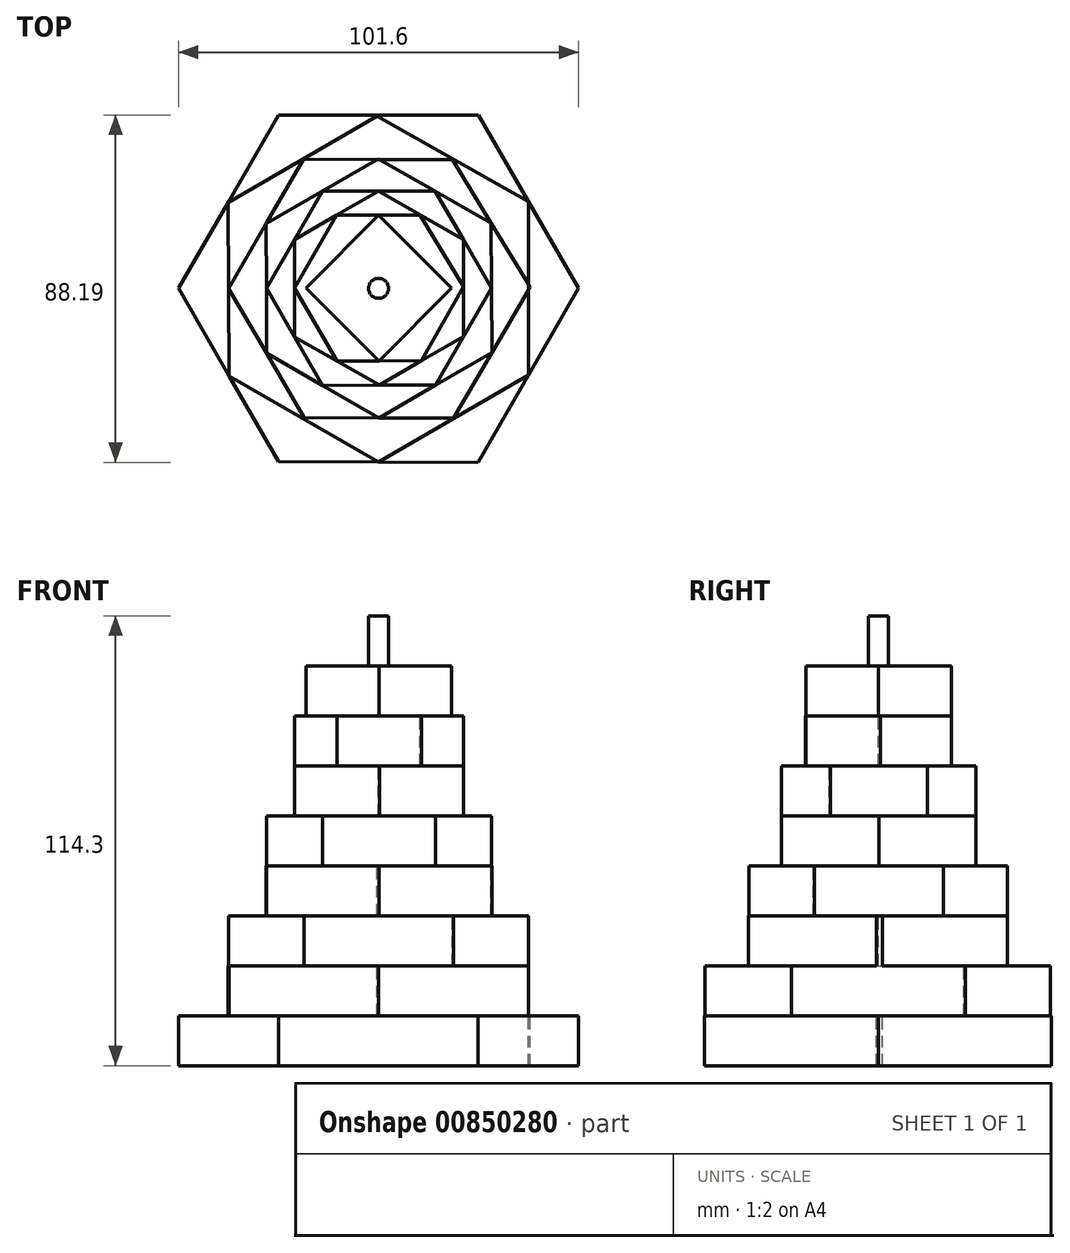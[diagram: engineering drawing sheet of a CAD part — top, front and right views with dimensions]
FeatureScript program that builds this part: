
annotation { "Feature Type Name" : "Feature", "Feature Type Description" : "" }
export const myFeature = defineFeature(function(context is Context, id is Id, definition is map)
    precondition{}
    {
        {
            var Q0;
            Q0=qCreatedBy(makeId("Top.planeOp"),FACE);
            var sketch = newSketch(context, id + "F0", { "sketchPlane" : qUnion([Q0])});
            skLineSegment(sketch, "E0.0", {"start": v(-25.4, 44) * mm, "end": v(25.4, 44) * mm});
            skLineSegment(sketch, "E0.1", {"start": v(25.4, 44) * mm, "end": v(50.8, 0) * mm});
            skLineSegment(sketch, "E0.2", {"start": v(50.8, 0) * mm, "end": v(25.22, -44.2) * mm});
            skLineSegment(sketch, "E0.3", {"start": v(25.22, -44.2) * mm, "end": v(-25.4, -44) * mm});
            skLineSegment(sketch, "E0.4", {"start": v(-25.4, -44) * mm, "end": v(-50.8, 0) * mm});
            skLineSegment(sketch, "E0.5", {"start": v(-50.8, 0) * mm, "end": v(-25.4, 44) * mm});
            skPoint(sketch, "E0.0.midPoint", {"position": v(0, 44) * mm});
            skLineSegment(sketch, "E1.0", {"start": v(-0.34, 43.7) * mm, "end": v(38.07, 22.05) * mm});
            skLineSegment(sketch, "E1.1", {"start": v(38.07, 22.05) * mm, "end": v(38.05, -22.04) * mm});
            skLineSegment(sketch, "E1.2", {"start": v(38.05, -22.04) * mm, "end": v(0.03, -44.1) * mm});
            skLineSegment(sketch, "E1.3", {"start": v(0.03, -44.1) * mm, "end": v(-37.96, -22.24) * mm});
            skLineSegment(sketch, "E1.4", {"start": v(-37.96, -22.24) * mm, "end": v(-38.26, 21.72) * mm});
            skLineSegment(sketch, "E1.5", {"start": v(-38.26, 21.72) * mm, "end": v(-0.34, 43.7) * mm});
            skPoint(sketch, "E1.0.midPoint", {"position": v(18.87, 32.87) * mm});
            skLineSegment(sketch, "E2.0", {"start": v(-19.09, 32.78) * mm, "end": v(18.8, 32.73) * mm});
            skLineSegment(sketch, "E2.1", {"start": v(18.8, 32.73) * mm, "end": v(38.5, 0.3) * mm});
            skLineSegment(sketch, "E2.2", {"start": v(38.5, 0.3) * mm, "end": v(19.06, -33.01) * mm});
            skLineSegment(sketch, "E2.3", {"start": v(19.06, -33.01) * mm, "end": v(-18.96, -32.83) * mm});
            skLineSegment(sketch, "E2.4", {"start": v(-18.96, -32.83) * mm, "end": v(-38.05, -0.06) * mm});
            skLineSegment(sketch, "E2.5", {"start": v(-38.05, -0.06) * mm, "end": v(-19.09, 32.78) * mm});
            skPoint(sketch, "E2.0.midPoint", {"position": v(-0.14, 32.75) * mm});
            skLineSegment(sketch, "E3.0", {"start": v(-28.53, 16.43) * mm, "end": v(-0.03, 32.94) * mm});
            skLineSegment(sketch, "E3.1", {"start": v(-0.03, 32.94) * mm, "end": v(28.62, 16.57) * mm});
            skLineSegment(sketch, "E3.2", {"start": v(28.62, 16.57) * mm, "end": v(28.82, -16.28) * mm});
            skLineSegment(sketch, "E3.3", {"start": v(28.82, -16.28) * mm, "end": v(0.07, -32.92) * mm});
            skLineSegment(sketch, "E3.4", {"start": v(0.07, -32.92) * mm, "end": v(-28.48, -16.5) * mm});
            skLineSegment(sketch, "E3.5", {"start": v(-28.48, -16.5) * mm, "end": v(-28.53, 16.43) * mm});
            skPoint(sketch, "E3.0.midPoint", {"position": v(-14.28, 24.69) * mm});
            skLineSegment(sketch, "E4.0", {"start": v(-14.2, 24.72) * mm, "end": v(14.35, 24.72) * mm});
            skLineSegment(sketch, "E4.1", {"start": v(14.35, 24.72) * mm, "end": v(28.72, 0.09) * mm});
            skLineSegment(sketch, "E4.2", {"start": v(28.72, 0.09) * mm, "end": v(14.47, -24.59) * mm});
            skLineSegment(sketch, "E4.3", {"start": v(14.47, -24.59) * mm, "end": v(-14.24, -24.69) * mm});
            skLineSegment(sketch, "E4.4", {"start": v(-14.24, -24.69) * mm, "end": v(-28.5, 0.02) * mm});
            skLineSegment(sketch, "E4.5", {"start": v(-28.5, 0.02) * mm, "end": v(-14.2, 24.72) * mm});
            skPoint(sketch, "E4.0.midPoint", {"position": v(0.08, 24.72) * mm});
            skLineSegment(sketch, "E5.0", {"start": v(0.02, 24.73) * mm, "end": v(21.52, 12.43) * mm});
            skLineSegment(sketch, "E5.1", {"start": v(21.52, 12.43) * mm, "end": v(21.6, -12.25) * mm});
            skLineSegment(sketch, "E5.2", {"start": v(21.6, -12.25) * mm, "end": v(0.2, -24.64) * mm});
            skLineSegment(sketch, "E5.3", {"start": v(0.2, -24.64) * mm, "end": v(-21.33, -12.4) * mm});
            skLineSegment(sketch, "E5.4", {"start": v(-21.33, -12.4) * mm, "end": v(-21.38, 12.32) * mm});
            skLineSegment(sketch, "E5.5", {"start": v(-21.38, 12.32) * mm, "end": v(0.02, 24.73) * mm});
            skPoint(sketch, "E5.0.midPoint", {"position": v(10.77, 18.58) * mm});
            skLineSegment(sketch, "E6.0", {"start": v(-10.63, 18.55) * mm, "end": v(10.57, 18.57) * mm});
            skLineSegment(sketch, "E6.1", {"start": v(10.57, 18.57) * mm, "end": v(21.56, 0.46) * mm});
            skLineSegment(sketch, "E6.2", {"start": v(21.56, 0.46) * mm, "end": v(10.94, -18.41) * mm});
            skLineSegment(sketch, "E6.3", {"start": v(10.94, -18.41) * mm, "end": v(-10.58, -18.52) * mm});
            skLineSegment(sketch, "E6.4", {"start": v(-10.58, -18.52) * mm, "end": v(-21.35, 0.03) * mm});
            skLineSegment(sketch, "E6.5", {"start": v(-21.35, 0.03) * mm, "end": v(-10.63, 18.55) * mm});
            skPoint(sketch, "E6.0.midPoint", {"position": v(-0.03, 18.56) * mm});
            skPoint(sketch, "E7.endSnap0", {"position": v(0.18, -18.46) * mm});
            skLineSegment(sketch, "E8.0", {"start": v(-0.03, 18.56) * mm, "end": v(18.59, 0.01) * mm});
            skLineSegment(sketch, "E8.1", {"start": v(18.59, 0.01) * mm, "end": v(0.18, -18.46) * mm});
            skLineSegment(sketch, "E8.2", {"start": v(0.18, -18.46) * mm, "end": v(-18.44, 0.09) * mm});
            skLineSegment(sketch, "E8.3", {"start": v(-18.44, 0.09) * mm, "end": v(-0.03, 18.56) * mm});
            skPoint(sketch, "E9", {"position": v(0, 0) * mm});
            skCircle(sketch, "E10", {"center": v(0, 0) * mm, "radius": 2.54 * mm});
            skSolve(sketch);
        }
        {
            var Q0;
            {var subQ3=sQuery(id+"F0.wireOp",EDGE,"E1.3");Q0=makeQuery(id+"F0.imprint","IMPRINT",FACE,{"disambiguationData":[TD([[makeQuery(id+"F0.imprint","IMPRINT",EDGE,{"derivedFrom":subQ3}),1.0]])]});}
            var Q1;
            {var subQ3=sQuery(id+"F0.wireOp",EDGE,"E1.2");Q1=makeQuery(id+"F0.imprint","IMPRINT",FACE,{"disambiguationData":[TD([[makeQuery(id+"F0.imprint","IMPRINT",EDGE,{"derivedFrom":subQ3}),1.0]])]});}
            var Q2;
            {var subQ11=sQuery(id+"F0.wireOp",EDGE,"E1.0");Q2=makeQuery(id+"F0.imprint","IMPRINT",FACE,{"disambiguationData":[TD([[makeQuery(id+"F0.imprint","IMPRINT",EDGE,{"derivedFrom":subQ11}),-1.0]])]});}
            var Q3;
            {var subQ0=sQuery(id+"F0.wireOp",EDGE,"E2.3");var subQ1=sQuery(id+"F0.wireOp",EDGE,"E2.2");var subQ2=makeQuery(id+"F0.imprint","INTERSECT",VERTEX,{"derivedFrom":[subQ1,subQ0]});Q3=makeQuery(id+"F0.imprint","IMPRINT",FACE,{"disambiguationData":[TD([[makeQuery(id+"F0.imprint","IMPRINT",EDGE,{"disambiguationData":[TD([[subQ2,1.0]])],"derivedFrom":subQ1}),-1.0]])]});}
            var Q4;
            {var subQ0=sQuery(id+"F0.wireOp",EDGE,"E2.4");var subQ1=sQuery(id+"F0.wireOp",EDGE,"E2.3");var subQ2=makeQuery(id+"F0.imprint","INTERSECT",VERTEX,{"derivedFrom":[subQ1,subQ0]});Q4=makeQuery(id+"F0.imprint","IMPRINT",FACE,{"disambiguationData":[TD([[makeQuery(id+"F0.imprint","IMPRINT",EDGE,{"disambiguationData":[TD([[subQ2,1.0]])],"derivedFrom":subQ1}),-1.0]])]});}
            var Q5;
            {var subQ0=sQuery(id+"F0.wireOp",EDGE,"E3.4");var subQ1=sQuery(id+"F0.wireOp",EDGE,"E3.3");var subQ2=makeQuery(id+"F0.imprint","INTERSECT",VERTEX,{"derivedFrom":[sQuery(id+"F0.wireOp",EDGE,"E2.3"),subQ1,subQ0]});Q5=makeQuery(id+"F0.imprint","IMPRINT",FACE,{"disambiguationData":[TD([[makeQuery(id+"F0.imprint","IMPRINT",EDGE,{"disambiguationData":[TD([[subQ2,1.0]])],"derivedFrom":subQ1}),-1.0]])]});}
            var Q6;
            {var subQ0=sQuery(id+"F0.wireOp",EDGE,"E4.4");var subQ1=sQuery(id+"F0.wireOp",EDGE,"E4.3");var subQ2=makeQuery(id+"F0.imprint","INTERSECT",VERTEX,{"derivedFrom":[sQuery(id+"F0.wireOp",EDGE,"E3.4"),subQ1,subQ0]});Q6=makeQuery(id+"F0.imprint","IMPRINT",FACE,{"disambiguationData":[TD([[makeQuery(id+"F0.imprint","IMPRINT",EDGE,{"disambiguationData":[TD([[subQ2,1.0]])],"derivedFrom":subQ1}),-1.0]])]});}
            var Q7;
            {var subQ0=sQuery(id+"F0.wireOp",EDGE,"E5.3");var subQ1=sQuery(id+"F0.wireOp",EDGE,"E5.2");var subQ2=makeQuery(id+"F0.imprint","INTERSECT",VERTEX,{"derivedFrom":[sQuery(id+"F0.wireOp",EDGE,"E4.3"),subQ1,subQ0]});Q7=makeQuery(id+"F0.imprint","IMPRINT",FACE,{"disambiguationData":[TD([[makeQuery(id+"F0.imprint","IMPRINT",EDGE,{"disambiguationData":[TD([[subQ2,1.0]])],"derivedFrom":subQ1}),-1.0]])]});}
            var Q8;
            {var subQ0=sQuery(id+"F0.wireOp",EDGE,"E4.3");var subQ1=sQuery(id+"F0.wireOp",EDGE,"E4.2");var subQ2=makeQuery(id+"F0.imprint","INTERSECT",VERTEX,{"derivedFrom":[sQuery(id+"F0.wireOp",EDGE,"E3.3"),subQ1,subQ0]});Q8=makeQuery(id+"F0.imprint","IMPRINT",FACE,{"disambiguationData":[TD([[makeQuery(id+"F0.imprint","IMPRINT",EDGE,{"disambiguationData":[TD([[subQ2,1.0]])],"derivedFrom":subQ1}),-1.0]])]});}
            var Q9;
            {var subQ3=sQuery(id+"F0.wireOp",EDGE,"E6.2");Q9=makeQuery(id+"F0.imprint","IMPRINT",FACE,{"disambiguationData":[TD([[makeQuery(id+"F0.imprint","IMPRINT",EDGE,{"derivedFrom":subQ3}),1.0]])]});}
            var Q10;
            {var subQ3=sQuery(id+"F0.wireOp",EDGE,"E6.1");Q10=makeQuery(id+"F0.imprint","IMPRINT",FACE,{"disambiguationData":[TD([[makeQuery(id+"F0.imprint","IMPRINT",EDGE,{"derivedFrom":subQ3}),-1.0]])]});}
            var Q11;
            {var subQ0=sQuery(id+"F0.wireOp",EDGE,"E3.3");var subQ1=sQuery(id+"F0.wireOp",EDGE,"E3.2");var subQ2=makeQuery(id+"F0.imprint","INTERSECT",VERTEX,{"derivedFrom":[sQuery(id+"F0.wireOp",EDGE,"E2.2"),subQ1,subQ0]});Q11=makeQuery(id+"F0.imprint","IMPRINT",FACE,{"disambiguationData":[TD([[makeQuery(id+"F0.imprint","IMPRINT",EDGE,{"disambiguationData":[TD([[subQ2,1.0]])],"derivedFrom":subQ1}),-1.0]])]});}
            var Q12;
            {var subQ0=sQuery(id+"F0.wireOp",EDGE,"E4.2");var subQ1=sQuery(id+"F0.wireOp",EDGE,"E4.1");var subQ2=makeQuery(id+"F0.imprint","INTERSECT",VERTEX,{"derivedFrom":[sQuery(id+"F0.wireOp",EDGE,"E3.2"),subQ1,subQ0]});Q12=makeQuery(id+"F0.imprint","IMPRINT",FACE,{"disambiguationData":[TD([[makeQuery(id+"F0.imprint","IMPRINT",EDGE,{"disambiguationData":[TD([[subQ2,1.0]])],"derivedFrom":subQ1}),-1.0]])]});}
            var Q13;
            {var subQ1=sQuery(id+"F0.wireOp",EDGE,"E2.1");var subQ6=sQuery(id+"F0.wireOp",EDGE,"E1.1");var subQ8=makeQuery(id+"F0.imprint","INTERSECT",VERTEX,{"derivedFrom":[subQ6,subQ1]});Q13=makeQuery(id+"F0.imprint","IMPRINT",FACE,{"disambiguationData":[TD([[makeQuery(id+"F0.imprint","IMPRINT",EDGE,{"disambiguationData":[TD([[subQ8,-1.0]])],"derivedFrom":subQ6}),-1.0]])]});}
            var Q14;
            {var subQ0=sQuery(id+"F0.wireOp",EDGE,"E3.2");var subQ1=sQuery(id+"F0.wireOp",EDGE,"E3.1");var subQ2=makeQuery(id+"F0.imprint","INTERSECT",VERTEX,{"derivedFrom":[sQuery(id+"F0.wireOp",EDGE,"E2.1"),subQ1,subQ0]});Q14=makeQuery(id+"F0.imprint","IMPRINT",FACE,{"disambiguationData":[TD([[makeQuery(id+"F0.imprint","IMPRINT",EDGE,{"disambiguationData":[TD([[subQ2,1.0]])],"derivedFrom":subQ1}),-1.0]])]});}
            var Q15;
            {var subQ0=sQuery(id+"F0.wireOp",EDGE,"E2.1");var subQ1=sQuery(id+"F0.wireOp",EDGE,"E2.0");var subQ2=makeQuery(id+"F0.imprint","INTERSECT",VERTEX,{"derivedFrom":[subQ1,subQ0]});Q15=makeQuery(id+"F0.imprint","IMPRINT",FACE,{"disambiguationData":[TD([[makeQuery(id+"F0.imprint","IMPRINT",EDGE,{"disambiguationData":[TD([[subQ2,1.0]])],"derivedFrom":subQ1}),-1.0]])]});}
            var Q16;
            {var subQ0=sQuery(id+"F0.wireOp",EDGE,"E2.5");var subQ1=sQuery(id+"F0.wireOp",EDGE,"E2.0");var subQ2=makeQuery(id+"F0.imprint","INTERSECT",VERTEX,{"derivedFrom":[subQ1,subQ0]});Q16=makeQuery(id+"F0.imprint","IMPRINT",FACE,{"disambiguationData":[TD([[makeQuery(id+"F0.imprint","IMPRINT",EDGE,{"disambiguationData":[TD([[subQ2,-1.0]])],"derivedFrom":subQ1}),-1.0]])]});}
            var Q17;
            {var subQ1=sQuery(id+"F0.wireOp",EDGE,"E3.0");var subQ8=sQuery(id+"F0.wireOp",EDGE,"E2.0");var subQ13=makeQuery(id+"F0.imprint","INTERSECT",VERTEX,{"derivedFrom":[subQ8,subQ1]});Q17=makeQuery(id+"F0.imprint","IMPRINT",FACE,{"disambiguationData":[TD([[makeQuery(id+"F0.imprint","IMPRINT",EDGE,{"disambiguationData":[TD([[subQ13,-1.0]])],"derivedFrom":subQ8}),-1.0]])]});}
            var Q18;
            {var subQ0=sQuery(id+"F0.wireOp",EDGE,"E4.5");var subQ1=sQuery(id+"F0.wireOp",EDGE,"E4.0");var subQ2=makeQuery(id+"F0.imprint","INTERSECT",VERTEX,{"derivedFrom":[subQ1,subQ0]});Q18=makeQuery(id+"F0.imprint","IMPRINT",FACE,{"disambiguationData":[TD([[makeQuery(id+"F0.imprint","IMPRINT",EDGE,{"disambiguationData":[TD([[subQ2,-1.0]])],"derivedFrom":subQ1}),-1.0]])]});}
            var Q19;
            {var subQ3=sQuery(id+"F0.wireOp",EDGE,"E6.5");Q19=makeQuery(id+"F0.imprint","IMPRINT",FACE,{"disambiguationData":[TD([[makeQuery(id+"F0.imprint","IMPRINT",EDGE,{"derivedFrom":subQ3}),1.0]])]});}
            var Q20;
            {var subQ1=sQuery(id+"F0.wireOp",EDGE,"E6.4");Q20=makeQuery(id+"F0.imprint","IMPRINT",FACE,{"disambiguationData":[TD([[makeQuery(id+"F0.imprint","IMPRINT",EDGE,{"derivedFrom":subQ1}),-1.0]])]});}
            var Q21;
            Q21=makeQuery(id+"F0.imprint","IMPRINT",FACE,{"disambiguationData":[TD([[makeQuery(id+"F0.imprint","IMPRINT",EDGE,{"derivedFrom":sQuery(id+"F0.wireOp",EDGE,"E8.0")}),-1.0]])]});
            var Q22;
            Q22=makeQuery(id+"F0.imprint","IMPRINT",FACE,{"disambiguationData":[TD([[makeQuery(id+"F0.imprint","IMPRINT",EDGE,{"derivedFrom":sQuery(id+"F0.wireOp",EDGE,"E10")}),1.0]])]});
            var Q23;
            {var subQ1=sQuery(id+"F0.wireOp",EDGE,"E4.0");var subQ3=sQuery(id+"F0.wireOp",EDGE,"E5.0");var subQ4=makeQuery(id+"F0.imprint","INTERSECT",VERTEX,{"derivedFrom":[subQ1,subQ3]});Q23=makeQuery(id+"F0.imprint","IMPRINT",FACE,{"disambiguationData":[TD([[makeQuery(id+"F0.imprint","IMPRINT",EDGE,{"disambiguationData":[TD([[subQ4,-1.0]])],"derivedFrom":subQ1}),-1.0]])]});}
            var Q24;
            {var subQ3=sQuery(id+"F0.wireOp",EDGE,"E6.1");Q24=makeQuery(id+"F0.imprint","IMPRINT",FACE,{"disambiguationData":[TD([[makeQuery(id+"F0.imprint","IMPRINT",EDGE,{"derivedFrom":subQ3}),1.0]])]});}
            var Q25;
            {var subQ0=sQuery(id+"F0.wireOp",EDGE,"E2.5");var subQ1=sQuery(id+"F0.wireOp",EDGE,"E2.4");var subQ2=makeQuery(id+"F0.imprint","INTERSECT",VERTEX,{"derivedFrom":[subQ1,subQ0]});Q25=makeQuery(id+"F0.imprint","IMPRINT",FACE,{"disambiguationData":[TD([[makeQuery(id+"F0.imprint","IMPRINT",EDGE,{"disambiguationData":[TD([[subQ2,1.0]])],"derivedFrom":subQ1}),-1.0]])]});}
            var Q26;
            {var subQ0=sQuery(id+"F0.wireOp",EDGE,"E3.5");var subQ1=sQuery(id+"F0.wireOp",EDGE,"E3.4");var subQ2=makeQuery(id+"F0.imprint","INTERSECT",VERTEX,{"derivedFrom":[sQuery(id+"F0.wireOp",EDGE,"E2.4"),subQ1,subQ0]});Q26=makeQuery(id+"F0.imprint","IMPRINT",FACE,{"disambiguationData":[TD([[makeQuery(id+"F0.imprint","IMPRINT",EDGE,{"disambiguationData":[TD([[subQ2,1.0]])],"derivedFrom":subQ1}),-1.0]])]});}
            var Q27;
            {var subQ0=sQuery(id+"F0.wireOp",EDGE,"E4.5");var subQ1=sQuery(id+"F0.wireOp",EDGE,"E4.4");var subQ2=makeQuery(id+"F0.imprint","INTERSECT",VERTEX,{"derivedFrom":[sQuery(id+"F0.wireOp",EDGE,"E3.5"),subQ1,subQ0]});Q27=makeQuery(id+"F0.imprint","IMPRINT",FACE,{"disambiguationData":[TD([[makeQuery(id+"F0.imprint","IMPRINT",EDGE,{"disambiguationData":[TD([[subQ2,1.0]])],"derivedFrom":subQ1}),-1.0]])]});}
            var Q28;
            {var subQ3=sQuery(id+"F0.wireOp",EDGE,"E6.4");Q28=makeQuery(id+"F0.imprint","IMPRINT",FACE,{"disambiguationData":[TD([[makeQuery(id+"F0.imprint","IMPRINT",EDGE,{"derivedFrom":subQ3}),1.0]])]});}
            var Q29;
            {var subQ3=sQuery(id+"F0.wireOp",EDGE,"E1.4");Q29=makeQuery(id+"F0.imprint","IMPRINT",FACE,{"disambiguationData":[TD([[makeQuery(id+"F0.imprint","IMPRINT",EDGE,{"derivedFrom":subQ3}),1.0]])]});}
            var Q30;
            {var subQ3=sQuery(id+"F0.wireOp",EDGE,"E2.2");var subQ7=sQuery(id+"F0.wireOp",EDGE,"E2.1");var subQ8=makeQuery(id+"F0.imprint","INTERSECT",VERTEX,{"derivedFrom":[subQ7,subQ3]});Q30=makeQuery(id+"F0.imprint","IMPRINT",FACE,{"disambiguationData":[TD([[makeQuery(id+"F0.imprint","IMPRINT",EDGE,{"disambiguationData":[TD([[subQ8,1.0]])],"derivedFrom":subQ7}),1.0]])]});}
            var Q31;
            {var subQ1=sQuery(id+"F0.wireOp",EDGE,"E0.0");Q31=makeQuery(id+"F0.imprint","IMPRINT",FACE,{"disambiguationData":[TD([[makeQuery(id+"F0.imprint","IMPRINT",EDGE,{"derivedFrom":subQ1}),-1.0]])]});}
            extrude(context, id + "F1", {"entities" : qUnion([Q0, Q1, Q2, Q3, Q4, Q5, Q6, Q7, Q8, Q9, Q10, Q11, Q12, Q13, Q14, Q15, Q16, Q17, Q18, Q19, Q20, Q21, Q22, Q23, Q24, Q25, Q26, Q27, Q28, Q29, Q30, Q31]), "oppositeDirection" : true, "depth" : 114.3 * mm, "offsetDistance" : 25.4 * mm});
        }
        {
            var Q0;
            {var subQ1=sQuery(id+"F0.wireOp",EDGE,"E0.0");Q0=makeQuery(id+"F0.imprint","IMPRINT",FACE,{"disambiguationData":[TD([[makeQuery(id+"F0.imprint","IMPRINT",EDGE,{"derivedFrom":subQ1}),-1.0]])]});}
            var Q1;
            {var subQ3=sQuery(id+"F0.wireOp",EDGE,"E1.2");Q1=makeQuery(id+"F0.imprint","IMPRINT",FACE,{"disambiguationData":[TD([[makeQuery(id+"F0.imprint","IMPRINT",EDGE,{"derivedFrom":subQ3}),1.0]])]});}
            var Q2;
            {var subQ3=sQuery(id+"F0.wireOp",EDGE,"E1.3");Q2=makeQuery(id+"F0.imprint","IMPRINT",FACE,{"disambiguationData":[TD([[makeQuery(id+"F0.imprint","IMPRINT",EDGE,{"derivedFrom":subQ3}),1.0]])]});}
            var Q3;
            {var subQ3=sQuery(id+"F0.wireOp",EDGE,"E1.4");Q3=makeQuery(id+"F0.imprint","IMPRINT",FACE,{"disambiguationData":[TD([[makeQuery(id+"F0.imprint","IMPRINT",EDGE,{"derivedFrom":subQ3}),1.0]])]});}
            var Q4;
            {var subQ3=sQuery(id+"F0.wireOp",EDGE,"E2.2");var subQ7=sQuery(id+"F0.wireOp",EDGE,"E2.1");var subQ8=makeQuery(id+"F0.imprint","INTERSECT",VERTEX,{"derivedFrom":[subQ7,subQ3]});Q4=makeQuery(id+"F0.imprint","IMPRINT",FACE,{"disambiguationData":[TD([[makeQuery(id+"F0.imprint","IMPRINT",EDGE,{"disambiguationData":[TD([[subQ8,1.0]])],"derivedFrom":subQ7}),1.0]])]});}
            extrude(context, id + "F2", {"entities" : qUnion([Q0, Q1, Q2, Q3, Q4]), "operationType" : NewBodyOperationType.REMOVE, "oppositeDirection" : true, "depth" : 101.6 * mm, "offsetDistance" : 25.4 * mm});
        }
        {
            var Q0;
            {var subQ11=sQuery(id+"F0.wireOp",EDGE,"E1.0");Q0=makeQuery(id+"F0.imprint","IMPRINT",FACE,{"disambiguationData":[TD([[makeQuery(id+"F0.imprint","IMPRINT",EDGE,{"derivedFrom":subQ11}),-1.0]])]});}
            extrude(context, id + "F3", {"entities" : qUnion([Q0]), "operationType" : NewBodyOperationType.REMOVE, "oppositeDirection" : true, "depth" : 88.9 * mm, "offsetDistance" : 25.4 * mm});
        }
        {
            var Q0;
            {var subQ0=sQuery(id+"F0.wireOp",EDGE,"E2.4");var subQ1=sQuery(id+"F0.wireOp",EDGE,"E2.3");var subQ2=makeQuery(id+"F0.imprint","INTERSECT",VERTEX,{"derivedFrom":[subQ1,subQ0]});Q0=makeQuery(id+"F0.imprint","IMPRINT",FACE,{"disambiguationData":[TD([[makeQuery(id+"F0.imprint","IMPRINT",EDGE,{"disambiguationData":[TD([[subQ2,1.0]])],"derivedFrom":subQ1}),-1.0]])]});}
            var Q1;
            {var subQ0=sQuery(id+"F0.wireOp",EDGE,"E2.3");var subQ1=sQuery(id+"F0.wireOp",EDGE,"E2.2");var subQ2=makeQuery(id+"F0.imprint","INTERSECT",VERTEX,{"derivedFrom":[subQ1,subQ0]});Q1=makeQuery(id+"F0.imprint","IMPRINT",FACE,{"disambiguationData":[TD([[makeQuery(id+"F0.imprint","IMPRINT",EDGE,{"disambiguationData":[TD([[subQ2,1.0]])],"derivedFrom":subQ1}),-1.0]])]});}
            var Q2;
            {var subQ1=sQuery(id+"F0.wireOp",EDGE,"E2.1");var subQ6=sQuery(id+"F0.wireOp",EDGE,"E1.1");var subQ8=makeQuery(id+"F0.imprint","INTERSECT",VERTEX,{"derivedFrom":[subQ6,subQ1]});Q2=makeQuery(id+"F0.imprint","IMPRINT",FACE,{"disambiguationData":[TD([[makeQuery(id+"F0.imprint","IMPRINT",EDGE,{"disambiguationData":[TD([[subQ8,-1.0]])],"derivedFrom":subQ6}),-1.0]])]});}
            var Q3;
            {var subQ0=sQuery(id+"F0.wireOp",EDGE,"E2.1");var subQ1=sQuery(id+"F0.wireOp",EDGE,"E2.0");var subQ2=makeQuery(id+"F0.imprint","INTERSECT",VERTEX,{"derivedFrom":[subQ1,subQ0]});Q3=makeQuery(id+"F0.imprint","IMPRINT",FACE,{"disambiguationData":[TD([[makeQuery(id+"F0.imprint","IMPRINT",EDGE,{"disambiguationData":[TD([[subQ2,1.0]])],"derivedFrom":subQ1}),-1.0]])]});}
            var Q4;
            {var subQ0=sQuery(id+"F0.wireOp",EDGE,"E2.5");var subQ1=sQuery(id+"F0.wireOp",EDGE,"E2.0");var subQ2=makeQuery(id+"F0.imprint","INTERSECT",VERTEX,{"derivedFrom":[subQ1,subQ0]});Q4=makeQuery(id+"F0.imprint","IMPRINT",FACE,{"disambiguationData":[TD([[makeQuery(id+"F0.imprint","IMPRINT",EDGE,{"disambiguationData":[TD([[subQ2,-1.0]])],"derivedFrom":subQ1}),-1.0]])]});}
            var Q5;
            {var subQ0=sQuery(id+"F0.wireOp",EDGE,"E2.5");var subQ1=sQuery(id+"F0.wireOp",EDGE,"E2.4");var subQ2=makeQuery(id+"F0.imprint","INTERSECT",VERTEX,{"derivedFrom":[subQ1,subQ0]});Q5=makeQuery(id+"F0.imprint","IMPRINT",FACE,{"disambiguationData":[TD([[makeQuery(id+"F0.imprint","IMPRINT",EDGE,{"disambiguationData":[TD([[subQ2,1.0]])],"derivedFrom":subQ1}),-1.0]])]});}
            extrude(context, id + "F4", {"entities" : qUnion([Q0, Q1, Q2, Q3, Q4, Q5]), "operationType" : NewBodyOperationType.REMOVE, "oppositeDirection" : true, "depth" : 76.2 * mm, "offsetDistance" : 25.4 * mm});
        }
        {
            var Q0;
            {var subQ1=sQuery(id+"F0.wireOp",EDGE,"E3.0");var subQ8=sQuery(id+"F0.wireOp",EDGE,"E2.0");var subQ13=makeQuery(id+"F0.imprint","INTERSECT",VERTEX,{"derivedFrom":[subQ8,subQ1]});Q0=makeQuery(id+"F0.imprint","IMPRINT",FACE,{"disambiguationData":[TD([[makeQuery(id+"F0.imprint","IMPRINT",EDGE,{"disambiguationData":[TD([[subQ13,-1.0]])],"derivedFrom":subQ8}),-1.0]])]});}
            var Q1;
            {var subQ0=sQuery(id+"F0.wireOp",EDGE,"E3.2");var subQ1=sQuery(id+"F0.wireOp",EDGE,"E3.1");var subQ2=makeQuery(id+"F0.imprint","INTERSECT",VERTEX,{"derivedFrom":[sQuery(id+"F0.wireOp",EDGE,"E2.1"),subQ1,subQ0]});Q1=makeQuery(id+"F0.imprint","IMPRINT",FACE,{"disambiguationData":[TD([[makeQuery(id+"F0.imprint","IMPRINT",EDGE,{"disambiguationData":[TD([[subQ2,1.0]])],"derivedFrom":subQ1}),-1.0]])]});}
            var Q2;
            {var subQ0=sQuery(id+"F0.wireOp",EDGE,"E3.3");var subQ1=sQuery(id+"F0.wireOp",EDGE,"E3.2");var subQ2=makeQuery(id+"F0.imprint","INTERSECT",VERTEX,{"derivedFrom":[sQuery(id+"F0.wireOp",EDGE,"E2.2"),subQ1,subQ0]});Q2=makeQuery(id+"F0.imprint","IMPRINT",FACE,{"disambiguationData":[TD([[makeQuery(id+"F0.imprint","IMPRINT",EDGE,{"disambiguationData":[TD([[subQ2,1.0]])],"derivedFrom":subQ1}),-1.0]])]});}
            var Q3;
            {var subQ0=sQuery(id+"F0.wireOp",EDGE,"E3.4");var subQ1=sQuery(id+"F0.wireOp",EDGE,"E3.3");var subQ2=makeQuery(id+"F0.imprint","INTERSECT",VERTEX,{"derivedFrom":[sQuery(id+"F0.wireOp",EDGE,"E2.3"),subQ1,subQ0]});Q3=makeQuery(id+"F0.imprint","IMPRINT",FACE,{"disambiguationData":[TD([[makeQuery(id+"F0.imprint","IMPRINT",EDGE,{"disambiguationData":[TD([[subQ2,1.0]])],"derivedFrom":subQ1}),-1.0]])]});}
            var Q4;
            {var subQ0=sQuery(id+"F0.wireOp",EDGE,"E3.5");var subQ1=sQuery(id+"F0.wireOp",EDGE,"E3.4");var subQ2=makeQuery(id+"F0.imprint","INTERSECT",VERTEX,{"derivedFrom":[sQuery(id+"F0.wireOp",EDGE,"E2.4"),subQ1,subQ0]});Q4=makeQuery(id+"F0.imprint","IMPRINT",FACE,{"disambiguationData":[TD([[makeQuery(id+"F0.imprint","IMPRINT",EDGE,{"disambiguationData":[TD([[subQ2,1.0]])],"derivedFrom":subQ1}),-1.0]])]});}
            extrude(context, id + "F5", {"entities" : qUnion([Q0, Q1, Q2, Q3, Q4]), "operationType" : NewBodyOperationType.REMOVE, "oppositeDirection" : true, "depth" : 63.5 * mm, "offsetDistance" : 25.4 * mm});
        }
        {
            var Q0;
            {var subQ0=sQuery(id+"F0.wireOp",EDGE,"E4.5");var subQ1=sQuery(id+"F0.wireOp",EDGE,"E4.0");var subQ2=makeQuery(id+"F0.imprint","INTERSECT",VERTEX,{"derivedFrom":[subQ1,subQ0]});Q0=makeQuery(id+"F0.imprint","IMPRINT",FACE,{"disambiguationData":[TD([[makeQuery(id+"F0.imprint","IMPRINT",EDGE,{"disambiguationData":[TD([[subQ2,-1.0]])],"derivedFrom":subQ1}),-1.0]])]});}
            var Q1;
            {var subQ1=sQuery(id+"F0.wireOp",EDGE,"E4.0");var subQ3=sQuery(id+"F0.wireOp",EDGE,"E5.0");var subQ4=makeQuery(id+"F0.imprint","INTERSECT",VERTEX,{"derivedFrom":[subQ1,subQ3]});Q1=makeQuery(id+"F0.imprint","IMPRINT",FACE,{"disambiguationData":[TD([[makeQuery(id+"F0.imprint","IMPRINT",EDGE,{"disambiguationData":[TD([[subQ4,-1.0]])],"derivedFrom":subQ1}),-1.0]])]});}
            var Q2;
            {var subQ0=sQuery(id+"F0.wireOp",EDGE,"E4.5");var subQ1=sQuery(id+"F0.wireOp",EDGE,"E4.4");var subQ2=makeQuery(id+"F0.imprint","INTERSECT",VERTEX,{"derivedFrom":[sQuery(id+"F0.wireOp",EDGE,"E3.5"),subQ1,subQ0]});Q2=makeQuery(id+"F0.imprint","IMPRINT",FACE,{"disambiguationData":[TD([[makeQuery(id+"F0.imprint","IMPRINT",EDGE,{"disambiguationData":[TD([[subQ2,1.0]])],"derivedFrom":subQ1}),-1.0]])]});}
            var Q3;
            {var subQ0=sQuery(id+"F0.wireOp",EDGE,"E4.4");var subQ1=sQuery(id+"F0.wireOp",EDGE,"E4.3");var subQ2=makeQuery(id+"F0.imprint","INTERSECT",VERTEX,{"derivedFrom":[sQuery(id+"F0.wireOp",EDGE,"E3.4"),subQ1,subQ0]});Q3=makeQuery(id+"F0.imprint","IMPRINT",FACE,{"disambiguationData":[TD([[makeQuery(id+"F0.imprint","IMPRINT",EDGE,{"disambiguationData":[TD([[subQ2,1.0]])],"derivedFrom":subQ1}),-1.0]])]});}
            var Q4;
            {var subQ0=sQuery(id+"F0.wireOp",EDGE,"E4.3");var subQ1=sQuery(id+"F0.wireOp",EDGE,"E4.2");var subQ2=makeQuery(id+"F0.imprint","INTERSECT",VERTEX,{"derivedFrom":[sQuery(id+"F0.wireOp",EDGE,"E3.3"),subQ1,subQ0]});Q4=makeQuery(id+"F0.imprint","IMPRINT",FACE,{"disambiguationData":[TD([[makeQuery(id+"F0.imprint","IMPRINT",EDGE,{"disambiguationData":[TD([[subQ2,1.0]])],"derivedFrom":subQ1}),-1.0]])]});}
            var Q5;
            {var subQ0=sQuery(id+"F0.wireOp",EDGE,"E4.2");var subQ1=sQuery(id+"F0.wireOp",EDGE,"E4.1");var subQ2=makeQuery(id+"F0.imprint","INTERSECT",VERTEX,{"derivedFrom":[sQuery(id+"F0.wireOp",EDGE,"E3.2"),subQ1,subQ0]});Q5=makeQuery(id+"F0.imprint","IMPRINT",FACE,{"disambiguationData":[TD([[makeQuery(id+"F0.imprint","IMPRINT",EDGE,{"disambiguationData":[TD([[subQ2,1.0]])],"derivedFrom":subQ1}),-1.0]])]});}
            extrude(context, id + "F6", {"entities" : qUnion([Q0, Q1, Q2, Q3, Q4, Q5]), "operationType" : NewBodyOperationType.REMOVE, "oppositeDirection" : true, "depth" : 50.8 * mm, "offsetDistance" : 25.4 * mm});
        }
        {
            var Q0;
            {var subQ3=sQuery(id+"F0.wireOp",EDGE,"E6.5");Q0=makeQuery(id+"F0.imprint","IMPRINT",FACE,{"disambiguationData":[TD([[makeQuery(id+"F0.imprint","IMPRINT",EDGE,{"derivedFrom":subQ3}),1.0]])]});}
            var Q1;
            {var subQ3=sQuery(id+"F0.wireOp",EDGE,"E6.1");Q1=makeQuery(id+"F0.imprint","IMPRINT",FACE,{"disambiguationData":[TD([[makeQuery(id+"F0.imprint","IMPRINT",EDGE,{"derivedFrom":subQ3}),1.0]])]});}
            var Q2;
            {var subQ3=sQuery(id+"F0.wireOp",EDGE,"E6.2");Q2=makeQuery(id+"F0.imprint","IMPRINT",FACE,{"disambiguationData":[TD([[makeQuery(id+"F0.imprint","IMPRINT",EDGE,{"derivedFrom":subQ3}),1.0]])]});}
            var Q3;
            {var subQ0=sQuery(id+"F0.wireOp",EDGE,"E5.3");var subQ1=sQuery(id+"F0.wireOp",EDGE,"E5.2");var subQ2=makeQuery(id+"F0.imprint","INTERSECT",VERTEX,{"derivedFrom":[sQuery(id+"F0.wireOp",EDGE,"E4.3"),subQ1,subQ0]});Q3=makeQuery(id+"F0.imprint","IMPRINT",FACE,{"disambiguationData":[TD([[makeQuery(id+"F0.imprint","IMPRINT",EDGE,{"disambiguationData":[TD([[subQ2,1.0]])],"derivedFrom":subQ1}),-1.0]])]});}
            var Q4;
            {var subQ3=sQuery(id+"F0.wireOp",EDGE,"E6.4");Q4=makeQuery(id+"F0.imprint","IMPRINT",FACE,{"disambiguationData":[TD([[makeQuery(id+"F0.imprint","IMPRINT",EDGE,{"derivedFrom":subQ3}),1.0]])]});}
            extrude(context, id + "F7", {"entities" : qUnion([Q0, Q1, Q2, Q3, Q4]), "operationType" : NewBodyOperationType.REMOVE, "oppositeDirection" : true, "depth" : 38.1 * mm, "offsetDistance" : 25.4 * mm});
        }
        {
            var Q0;
            {var subQ1=sQuery(id+"F0.wireOp",EDGE,"E6.4");Q0=makeQuery(id+"F0.imprint","IMPRINT",FACE,{"disambiguationData":[TD([[makeQuery(id+"F0.imprint","IMPRINT",EDGE,{"derivedFrom":subQ1}),-1.0]])]});}
            var Q1;
            {var subQ3=sQuery(id+"F0.wireOp",EDGE,"E6.1");Q1=makeQuery(id+"F0.imprint","IMPRINT",FACE,{"disambiguationData":[TD([[makeQuery(id+"F0.imprint","IMPRINT",EDGE,{"derivedFrom":subQ3}),-1.0]])]});}
            extrude(context, id + "F8", {"entities" : qUnion([Q0, Q1]), "operationType" : NewBodyOperationType.REMOVE, "oppositeDirection" : true, "depth" : 25.4 * mm, "offsetDistance" : 25.4 * mm});
        }
        {
            var Q0;
            Q0=makeQuery(id+"F0.imprint","IMPRINT",FACE,{"disambiguationData":[TD([[makeQuery(id+"F0.imprint","IMPRINT",EDGE,{"derivedFrom":sQuery(id+"F0.wireOp",EDGE,"E8.0")}),-1.0]])]});
            extrude(context, id + "F9", {"entities" : qUnion([Q0]), "operationType" : NewBodyOperationType.REMOVE, "oppositeDirection" : true, "depth" : 12.7 * mm, "offsetDistance" : 25.4 * mm});
        }
    });
